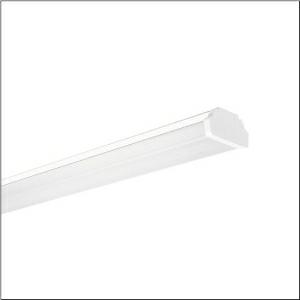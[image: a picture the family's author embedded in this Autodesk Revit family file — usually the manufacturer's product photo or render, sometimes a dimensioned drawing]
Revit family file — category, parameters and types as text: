
# Revit family: dus_r__31_ho_53bd812d2v6120_f11a
name_source: partatom
category: Lighting Fixtures
units: mm (PartAtom-declared; Revit-internal decimal feet)

## family parameters
Cut with Voids When Loaded = No
Host = Face
Light Source = No
Part Type = Normal
Room Calculation Point = No
Round Connector Dimension = Use Diameter
Shared = No

## types (1)
- --- (1 x LED, 12400 lm, 79.5 W, 6500K)
    Apparent Load = 80 VA
    CIE Flux Codes = 47 80 95 92 100
    Color Rendering = 80
    Color Temperature = 6500K
    Default Elevation = 1800 mm
    Description = DUS® 31 HOluminaire insert, length: 1.535mm, width: 81mm, height: 90mm, LED rated luminous flux: 12.400lm, light colour: 865, control gear: DALI 2, control gear: ECG DALI, with plug, 5-pole, with phase selection, mains connection: 220..240V, AC, 50/60Hz, primary optical cover: cover, of PMMA, light emission: direct distribution, primary light characteristic: symmetric, protection rating (complete): IP20, protection rating (LED compartment): IP50, insulation class (complete): insulation class I (protective earthing), certification: CE, ENEC, VDE, permissible ambient temperature for indoor applications: -25..+30°C, corresponds to IFS (International Featured Standards) requirements for safety and quality in the food industry, reducing of maximum allowable ambient temperature of 5°C with ceiling mounting, packaging unit: 1 piece
    Height = 95 mm
    Lamp = 1 x LED
    Lamp Light Flux = 12400 lm
    Lamp Power = 79.5 W
    Lamp count = 1
    Length = 1535 mm
    Luminous efficacy = 156 lm/W
    Manufacturer = Siteco
    ModVariant = No
    Model = 53BD812D2V6120
    Mounting Place = Ceiling
    Mounting Type = Pendant
    Number of Poles = 1
    OnlyDefault = Yes
    Power Factor = 1
    Product Name = DUS® 31 HO
    Product group = luminaire insert
    ProductGroupID = 902
    Protection Class = Protection class I
    Protection Degree = IP 20
    RLX_Detail_Level = 1
    RlxData = <blob elided: 41761 chars, md5=54d7ed86>
    Socket = socket
    Standby Power = 0 W
    System Light Flux = 12400 lm
    System Power = 80 W
    Type Comments = factory setting: luminous flux: 100 % | dim-lin: 254 | 345 mA
    Type Image = l_1003451.jpg
    URL = http://relux.com
    VarID = @adj_133503
    Voltage = 0 V
    Weight = 0.00 kg
    Width = 81 mm

## geometry (parser evidence)
native form markers: Blend x4, Sweep x11
no freeform markers — native parametric forms only
